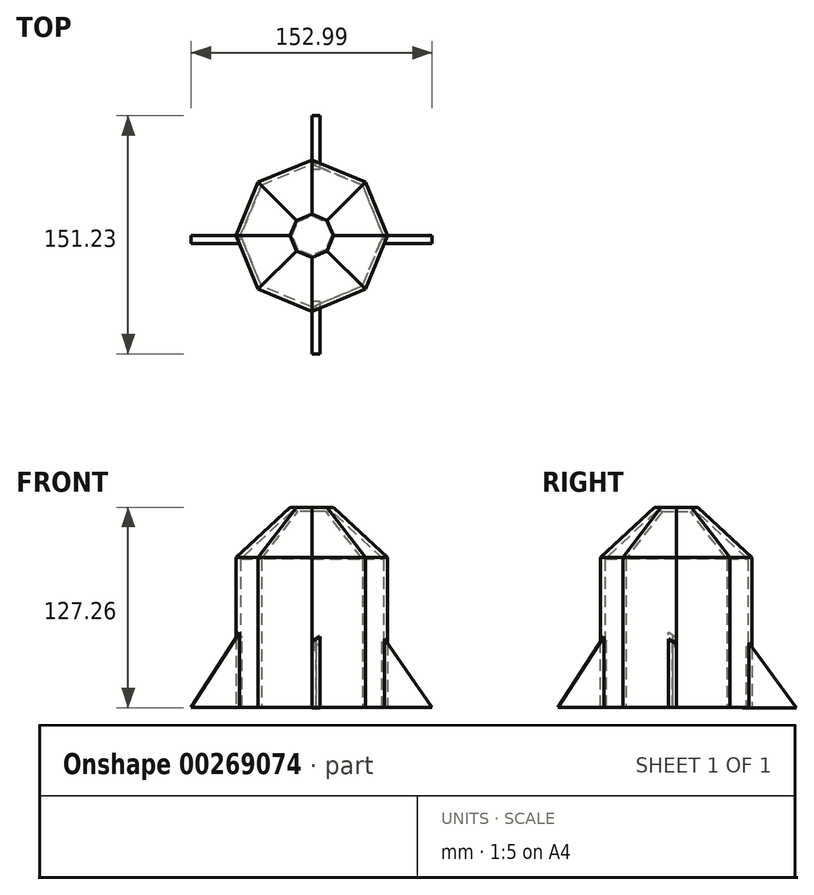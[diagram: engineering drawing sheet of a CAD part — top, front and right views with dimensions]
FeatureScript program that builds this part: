
annotation { "Feature Type Name" : "Feature", "Feature Type Description" : "" }
export const myFeature = defineFeature(function(context is Context, id is Id, definition is map)
    precondition{}
    {
        {
            var Q0;
            Q0=qCreatedBy(makeId("Top.planeOp"),FACE);
            var sketch = newSketch(context, id + "F0", { "sketchPlane" : qUnion([Q0])});
            skCircle(sketch, "E0.cCircle", {"center": v(0, 0) * mm, "radius": 48.11 * mm, "construction": true});
            skLineSegment(sketch, "E0.0", {"start": v(0, 48.11) * mm, "end": v(34.02, 34.02) * mm});
            skLineSegment(sketch, "E0.1", {"start": v(34.02, 34.02) * mm, "end": v(48.11, 0) * mm});
            skLineSegment(sketch, "E0.2", {"start": v(48.11, 0) * mm, "end": v(34.02, -34.02) * mm});
            skLineSegment(sketch, "E0.3", {"start": v(34.02, -34.02) * mm, "end": v(0, -48.11) * mm});
            skLineSegment(sketch, "E0.4", {"start": v(0, -48.11) * mm, "end": v(-34.02, -34.02) * mm});
            skLineSegment(sketch, "E0.5", {"start": v(-34.02, -34.02) * mm, "end": v(-48.11, 0) * mm});
            skLineSegment(sketch, "E0.6", {"start": v(-48.11, 0) * mm, "end": v(-34.02, 34.02) * mm});
            skLineSegment(sketch, "E0.7", {"start": v(-34.02, 34.02) * mm, "end": v(0, 48.11) * mm});
            skSolve(sketch);
        }
        {
            var Q0;
            Q0=makeQuery(id+"F0.imprint","IMPRINT",FACE,{"disambiguationData":[TD([[makeQuery(id+"F0.imprint","IMPRINT",EDGE,{"derivedFrom":sQuery(id+"F0.wireOp",EDGE,"E0.0")}),-1.0]])]});
            extrude(context, id + "F1", {"entities" : qUnion([Q0]), "depth" : 76.2 * mm});
        }
        {
            var Q0;
            Q0=makeQuery(id+"F1.opExtrude","CAP_FACE",FACE,{"disambiguationData":[OSD([sQuery(id+"F0.wireOp",EDGE,"E0.0"),sQuery(id+"F0.wireOp",EDGE,"E0.1"),sQuery(id+"F0.wireOp",EDGE,"E0.2"),sQuery(id+"F0.wireOp",EDGE,"E0.3"),sQuery(id+"F0.wireOp",EDGE,"E0.4"),sQuery(id+"F0.wireOp",EDGE,"E0.5"),sQuery(id+"F0.wireOp",EDGE,"E0.6"),sQuery(id+"F0.wireOp",EDGE,"E0.7")])],"isStart":false});
            var sketch = newSketch(context, id + "F2", { "sketchPlane" : qUnion([Q0])});
            skCircle(sketch, "E1.cCircle", {"center": v(0, 0) * mm, "radius": 48.11 * mm, "construction": true});
            skLineSegment(sketch, "E1.0", {"start": v(-34.02, 34.02) * mm, "end": v(0, 48.11) * mm});
            skLineSegment(sketch, "E1.1", {"start": v(0, 48.11) * mm, "end": v(34.02, 34.02) * mm});
            skLineSegment(sketch, "E1.2", {"start": v(34.02, 34.02) * mm, "end": v(48.11, 0) * mm});
            skLineSegment(sketch, "E1.3", {"start": v(48.11, 0) * mm, "end": v(34.02, -34.02) * mm});
            skLineSegment(sketch, "E1.4", {"start": v(34.02, -34.02) * mm, "end": v(0, -48.11) * mm});
            skLineSegment(sketch, "E1.5", {"start": v(0, -48.11) * mm, "end": v(-34.02, -34.02) * mm});
            skLineSegment(sketch, "E1.6", {"start": v(-34.02, -34.02) * mm, "end": v(-48.11, 0) * mm});
            skLineSegment(sketch, "E1.7", {"start": v(-48.11, 0) * mm, "end": v(-34.02, 34.02) * mm});
            skSolve(sketch);
        }
        {
            var Q0;
            Q0 = qSketchRegion(id + "F2", true);
            var Q1;
            Q1 = qConstructionFilter(qBodyType(qCreatedBy(id + "F2" ,EDGE), BodyType.WIRE), ConstructionObject.NO);
            extrude(context, id + "F3", {"entities" : qUnion([Q0]), "surfaceEntities" : qUnion([Q1]), "depth" : 50.8 * mm});
        }
        {
            var Q0;
            Q0=makeQuery(id+"F3.opExtrude","CAP_FACE",FACE,{"disambiguationData":[OSD([sQuery(id+"F2.wireOp",EDGE,"E1.0"),sQuery(id+"F2.wireOp",EDGE,"E1.1"),sQuery(id+"F2.wireOp",EDGE,"E1.2"),sQuery(id+"F2.wireOp",EDGE,"E1.3"),sQuery(id+"F2.wireOp",EDGE,"E1.4"),sQuery(id+"F2.wireOp",EDGE,"E1.5"),sQuery(id+"F2.wireOp",EDGE,"E1.6"),sQuery(id+"F2.wireOp",EDGE,"E1.7")])],"isStart":false});
            chamfer(context, id + "F4", {"entities" : qUnion([Q0]), "width" : 31.75 * mm, "tangentPropagation" : true});
        }
        {
            var Q0;
            Q0=qCreatedBy(makeId("Front.planeOp"),FACE);
            var sketch = newSketch(context, id + "F5", { "sketchPlane" : qUnion([Q0])});
            skLineSegment(sketch, "E2", {"start": v(-43.91, 50.7) * mm, "end": v(-43.91, 0) * mm});
            skLineSegment(sketch, "E3", {"start": v(-43.91, 50.7) * mm, "end": v(-76.6, 0) * mm});
            skLineSegment(sketch, "E4", {"start": v(-43.91, 0) * mm, "end": v(-76.6, 0) * mm});
            skSolve(sketch);
        }
        {
            var Q0;
            Q0=makeQuery(id+"F5.imprint","IMPRINT",FACE,{"disambiguationData":[TD([[makeQuery(id+"F5.imprint","IMPRINT",EDGE,{"derivedFrom":sQuery(id+"F5.wireOp",EDGE,"E2")}),-1.0]])]});
            extrude(context, id + "F6", {"entities" : qUnion([Q0]), "depth" : 5.08 * mm});
        }
        {
            var Q0;
            Q0=qCreatedBy(makeId("Right.planeOp"),FACE);
            var sketch = newSketch(context, id + "F7", { "sketchPlane" : qUnion([Q0])});
            skLineSegment(sketch, "E5", {"start": v(-41.76, 51.58) * mm, "end": v(-41.76, -0.15) * mm});
            skLineSegment(sketch, "E6", {"start": v(-41.76, 51.58) * mm, "end": v(-75.1, -0.15) * mm});
            skLineSegment(sketch, "E7", {"start": v(-41.76, -0.15) * mm, "end": v(-75.1, -0.15) * mm});
            skSolve(sketch);
        }
        {
            var Q0;
            Q0=makeQuery(id+"F7.imprint","IMPRINT",FACE,{"disambiguationData":[TD([[makeQuery(id+"F7.imprint","IMPRINT",EDGE,{"derivedFrom":sQuery(id+"F7.wireOp",EDGE,"E5")}),-1.0]])]});
            extrude(context, id + "F8", {"entities" : qUnion([Q0]), "depth" : 5.08 * mm});
        }
        {
            var Q0;
            Q0=qCreatedBy(makeId("Front.planeOp"),FACE);
            var sketch = newSketch(context, id + "F9", { "sketchPlane" : qUnion([Q0])});
            skLineSegment(sketch, "E8", {"start": v(44.25, 45.92) * mm, "end": v(44.25, 0) * mm});
            skLineSegment(sketch, "E9", {"start": v(44.25, 45.92) * mm, "end": v(76.4, 0) * mm});
            skLineSegment(sketch, "E10", {"start": v(76.4, 0) * mm, "end": v(44.25, 0) * mm});
            skSolve(sketch);
        }
        {
            var Q0;
            Q0=makeQuery(id+"F9.imprint","IMPRINT",FACE,{"disambiguationData":[TD([[makeQuery(id+"F9.imprint","IMPRINT",EDGE,{"derivedFrom":sQuery(id+"F9.wireOp",EDGE,"E8")}),1.0]])]});
            extrude(context, id + "F10", {"entities" : qUnion([Q0]), "depth" : 5.08 * mm});
        }
        {
            var Q0;
            Q0=qCreatedBy(makeId("Right.planeOp"),FACE);
            var sketch = newSketch(context, id + "F11", { "sketchPlane" : qUnion([Q0])});
            skLineSegment(sketch, "E11", {"start": v(41.96, 46.26) * mm, "end": v(41.96, -0.26) * mm});
            skLineSegment(sketch, "E12", {"start": v(41.96, 46.26) * mm, "end": v(76.13, -0.26) * mm});
            skLineSegment(sketch, "E13", {"start": v(76.13, -0.26) * mm, "end": v(41.96, -0.26) * mm});
            skSolve(sketch);
        }
        {
            var Q0;
            Q0=makeQuery(id+"F11.imprint","IMPRINT",FACE,{"disambiguationData":[TD([[makeQuery(id+"F11.imprint","IMPRINT",EDGE,{"derivedFrom":sQuery(id+"F11.wireOp",EDGE,"E11")}),1.0]])]});
            extrude(context, id + "F12", {"entities" : qUnion([Q0]), "depth" : 5.08 * mm});
        }
        {
            var Q0;
            Q0=makeQuery(id+"F1.opExtrude","SWEPT_BODY",BODY,{"disambiguationData":[OSD([sQuery(id+"F0.wireOp",EDGE,"E0.0"),sQuery(id+"F0.wireOp",EDGE,"E0.1"),sQuery(id+"F0.wireOp",EDGE,"E0.2"),sQuery(id+"F0.wireOp",EDGE,"E0.3"),sQuery(id+"F0.wireOp",EDGE,"E0.4"),sQuery(id+"F0.wireOp",EDGE,"E0.5"),sQuery(id+"F0.wireOp",EDGE,"E0.6"),sQuery(id+"F0.wireOp",EDGE,"E0.7")])]});
            var Q1;
            Q1=makeQuery(id+"F3.opExtrude","SWEPT_BODY",BODY,{"disambiguationData":[OSD([sQuery(id+"F2.wireOp",EDGE,"E1.0"),sQuery(id+"F2.wireOp",EDGE,"E1.1"),sQuery(id+"F2.wireOp",EDGE,"E1.2"),sQuery(id+"F2.wireOp",EDGE,"E1.3"),sQuery(id+"F2.wireOp",EDGE,"E1.4"),sQuery(id+"F2.wireOp",EDGE,"E1.5"),sQuery(id+"F2.wireOp",EDGE,"E1.6"),sQuery(id+"F2.wireOp",EDGE,"E1.7")])]});
            var Q2;
            Q2=makeQuery(id+"F6.opExtrude","SWEPT_BODY",BODY,{"disambiguationData":[OSD([sQuery(id+"F5.wireOp",EDGE,"E2"),sQuery(id+"F5.wireOp",EDGE,"E3"),sQuery(id+"F5.wireOp",EDGE,"E4")])]});
            var Q3;
            Q3=makeQuery(id+"F8.opExtrude","SWEPT_BODY",BODY,{"disambiguationData":[OSD([sQuery(id+"F7.wireOp",EDGE,"E5"),sQuery(id+"F7.wireOp",EDGE,"E6"),sQuery(id+"F7.wireOp",EDGE,"E7")])]});
            var Q4;
            Q4=makeQuery(id+"F10.opExtrude","SWEPT_BODY",BODY,{"disambiguationData":[OSD([sQuery(id+"F9.wireOp",EDGE,"E8"),sQuery(id+"F9.wireOp",EDGE,"E9"),sQuery(id+"F9.wireOp",EDGE,"E10")])]});
            var Q5;
            Q5=makeQuery(id+"F12.opExtrude","SWEPT_BODY",BODY,{"disambiguationData":[OSD([sQuery(id+"F11.wireOp",EDGE,"E11"),sQuery(id+"F11.wireOp",EDGE,"E12"),sQuery(id+"F11.wireOp",EDGE,"E13")])]});
            booleanBodies(context, id + "F13", {"operationType" : BooleanOperationType.UNION, "tools" : qUnion([Q0, Q1, Q2, Q3, Q4, Q5])});
        }
        {
            var Q0;
            Q0=makeQuery(id+"F13.opBoolean","MERGE",FACE,{"derivedFrom":[makeQuery(id+"F1.opExtrude","CAP_FACE",FACE,{"disambiguationData":[OSD([sQuery(id+"F0.wireOp",EDGE,"E0.0"),sQuery(id+"F0.wireOp",EDGE,"E0.1"),sQuery(id+"F0.wireOp",EDGE,"E0.2"),sQuery(id+"F0.wireOp",EDGE,"E0.3"),sQuery(id+"F0.wireOp",EDGE,"E0.4"),sQuery(id+"F0.wireOp",EDGE,"E0.5"),sQuery(id+"F0.wireOp",EDGE,"E0.6"),sQuery(id+"F0.wireOp",EDGE,"E0.7")])],"isStart":true}),makeQuery(id+"F6.opExtrude","SWEPT_FACE",FACE,{"disambiguationData":[OSD([sQuery(id+"F5.wireOp",EDGE,"E4")])]}),makeQuery(id+"F10.opExtrude","SWEPT_FACE",FACE,{"disambiguationData":[OSD([sQuery(id+"F9.wireOp",EDGE,"E10")])]})]});
            shell(context, id + "F14", {"entities" : qUnion([Q0]), "thickness" : 2.54 * mm});
        }
    });
